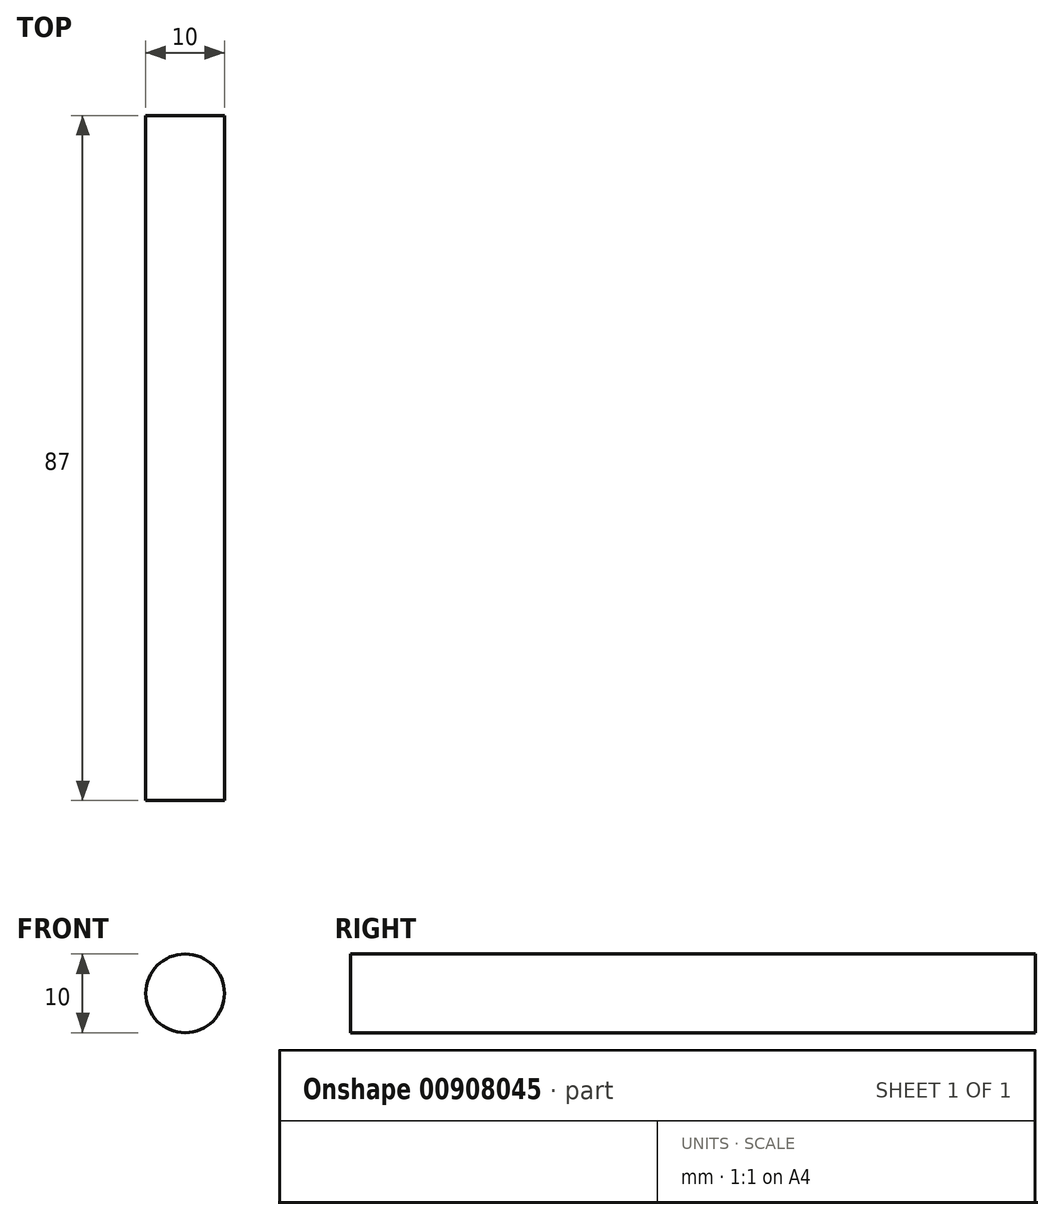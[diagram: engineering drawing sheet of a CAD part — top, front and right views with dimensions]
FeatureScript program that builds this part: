
annotation { "Feature Type Name" : "Feature", "Feature Type Description" : "" }
export const myFeature = defineFeature(function(context is Context, id is Id, definition is map)
    precondition{}
    {
        {
            var Q0;
            Q0=qCreatedBy(makeId("Front.planeOp"),FACE);
            var sketch = newSketch(context, id + "F0", { "sketchPlane" : qUnion([Q0])});
            skCircle(sketch, "E0", {"center": v(0, 0) * mm, "radius": 5 * mm});
            skSolve(sketch);
        }
        {
            var Q0;
            Q0=qSketchRegion(id+"F0",true);
            extrude(context, id + "F1", {"entities" : qUnion([Q0]), "depth" : 87 * mm, "offsetDistance" : 25 * mm});
        }
    });
